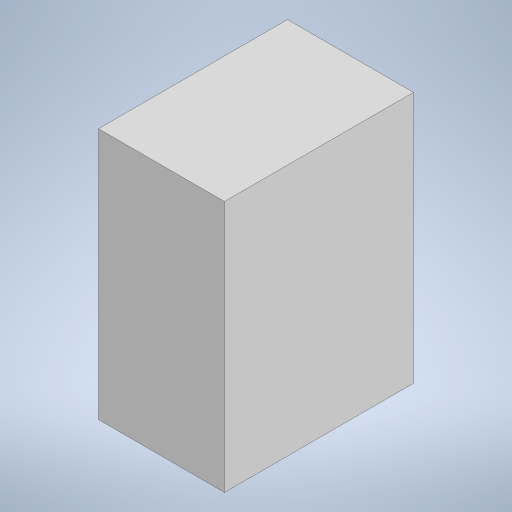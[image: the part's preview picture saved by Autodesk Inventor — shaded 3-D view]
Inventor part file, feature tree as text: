
AUTODESK INVENTOR PART (.ipt)
format: ipt  version: 2023 (Build 270158000, 158)  size: 208,384 bytes
history: native  units: in
note: dims shown in document units (in); Inventor stores cm internally (conversion verified against a paired STEP export)
features: extrude x4, sketch x3
ambient origin geometry x8: Origin, YZ Plane, XZ Plane, XY Plane, X Axis, Y Axis, Z Axis, Center Point
bodies: Solid1 (feature_tree)
feature tree (7):
  sketch  "Sketch1"  dims[d0=0.5in d1=1.0in]
  extrude  "Extrusion1"  Depth=1.0in
  extrude  "Extrusion4"  Depth=0.5in
  extrude  "Extrusion5"  Depth=2.0in TaperAngle=0.0deg
  sketch  "Sketch3"  dims[d2=1.5in d3=0.5in]
  extrude  "Extrusion6"  Depth=1.75in TaperAngle=0.0deg
  sketch  "Sketch4"  dims[d4=0.5in d5=2.0in d6=0.0in d21=1.75in d22=0.0in d23=0.125in d24=0.125in d25=1.0in d26=0.5in d27=0.5in d28=0.0in d29=0.5in d30=0.125in d31=0.125in d32=1.0in d34=0.0in d35=1.0in]
